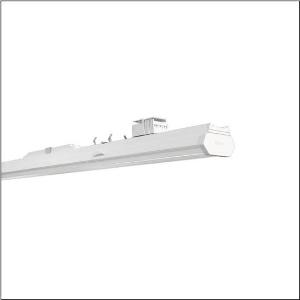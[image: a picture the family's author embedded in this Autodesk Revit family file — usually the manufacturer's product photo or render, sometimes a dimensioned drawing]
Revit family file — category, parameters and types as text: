
# Revit family: licross_r__11_protected_tw_51td1btnt8xx_5d1b
name_source: partatom
category: Lighting Fixtures
units: mm (PartAtom-declared; Revit-internal decimal feet)

## family parameters
Cut with Voids When Loaded = No
Host = Face
Light Source = No
Part Type = Normal
Room Calculation Point = No
Round Connector Dimension = Use Diameter
Shared = No

## types (1)
- --- (1 x LED 2700 K ... 6500 K, 8450 lm, 56 W, 2700K)
    Apparent Load = 56 VA
    CIE Flux Codes = 54 82 95 97 100
    Color Rendering = 80
    Color Temperature = 2700K
    Default Elevation = 1800 mm
    Description = Licross® 11 Protected TW, luminaire insert, of sheet steel, galvanised, coil coated, white, length: 1.500mm, width: 90mm, height: 101mm, LED rated luminous flux: 8.450lm, light colour: 8tw, control gear: DALI DT8, with plug, 5-pole, with phase selection, mains connection: 220..240V, AC, 50/60Hz, rated input power: 56W, halogen-free wiring, primary optical cover: cover, of PMMA, light emission: direct distribution, primary light characteristic: symmetric, protection rating (complete): IP54, insulation class (complete): insulation class I (protective earthing), certification: CE, ENEC, VDE, UKCA, protection symbol: D if used in an environment with non-conductive dust loads with corresponding accessories, impact resistance: IK06, permissible ambient temperature for indoor applications: -25..+35°C, corresponds to IFS (International Featured Standards) requirements for safety and quality in the food industry, reducing of maximum allowable ambient temperature of 5°C with ceiling mounting, LABS conformity tested according to VDMA 24364:2018-05, packaging unit: 1 piece
    Height = 92 mm
    Lamp = 1 x LED 2700 K ... 6500 K
    Lamp Light Flux = 8450 lm
    Lamp Power = 56 W
    Lamp count = 1
    Length = 1500 mm
    Luminous efficacy = 151 lm/W
    Manufacturer = Siteco
    ModVariant = No
    Model = 51TD1BTNT8XX
    Mounting Place = Ceiling
    Mounting Type = Pendant
    Number of Poles = 1
    OnlyDefault = Yes
    Power Factor = 1
    Product Name = Licross® 11 Protected TW
    Product group = luminaire insert
    ProductGroupID = 901
    Protection Class = Protection class I
    Protection Degree = IP 54
    RLX_Detail_Level = 1
    RLX_Emergency_Light_Flux = 0 lm
    RLX_Emergency_Type = 0
    RLX_Emergency_Type_DB = No
    RlxData = <blob elided: 20565 chars, md5=3eea2d12>
    Socket = socket
    Standby Power = 0 W
    System Light Flux = 8450 lm
    System Power = 56 W
    Type Comments = individual setting: CCT=2700K
    Type Image = l_1256145.jpg
    URL = http://relux.com
    VarID = @adj_015863
    Voltage = 0 V
    Weight = 0.00 kg
    Width = 88 mm

## geometry (parser evidence)
native form markers: Blend x4, Sweep x12
no freeform markers — native parametric forms only
